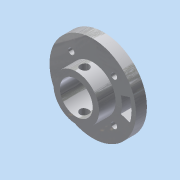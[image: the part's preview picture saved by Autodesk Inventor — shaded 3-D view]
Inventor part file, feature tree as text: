
AUTODESK INVENTOR PART (.ipt)
format: ipt  version: 2015 (Build 190159000, 159)  size: 182,784 bytes
history: native  units: in
note: dims shown in document units (in); Inventor stores cm internally (conversion verified against a paired STEP export)
features: other x4, extrude x3, sketch x3
ambient origin geometry x8: Origin, YZ Plane, XZ Plane, XY Plane, X Axis, Y Axis, Z Axis, Center Point
bodies: Solid1 (feature_tree)
feature tree (10):
  other  "StatorCore.ipt"
  extrude  "Extrusion1"  Depth=0.3937in
  extrude  "Extrusion2"  Depth=0.25in
  extrude  "Extrusion3"  Depth=0.201in
  other  "TaggingFeature1"
  sketch  "Sketch1"  dims[d0=0.3937in d1=0.748in]
  sketch  "Sketch2"  dims[d2=0.25in d3=0.0in d4=0.25in]
  sketch  "Sketch3"  dims[d5=0.375in d6=0.0in d7=0.201in d8=0.1875in d9=0.375in d10=0.0in d11=1.9685in]
  other  "Solid1::StatorCore.ipt"
  other  "Srf1"
